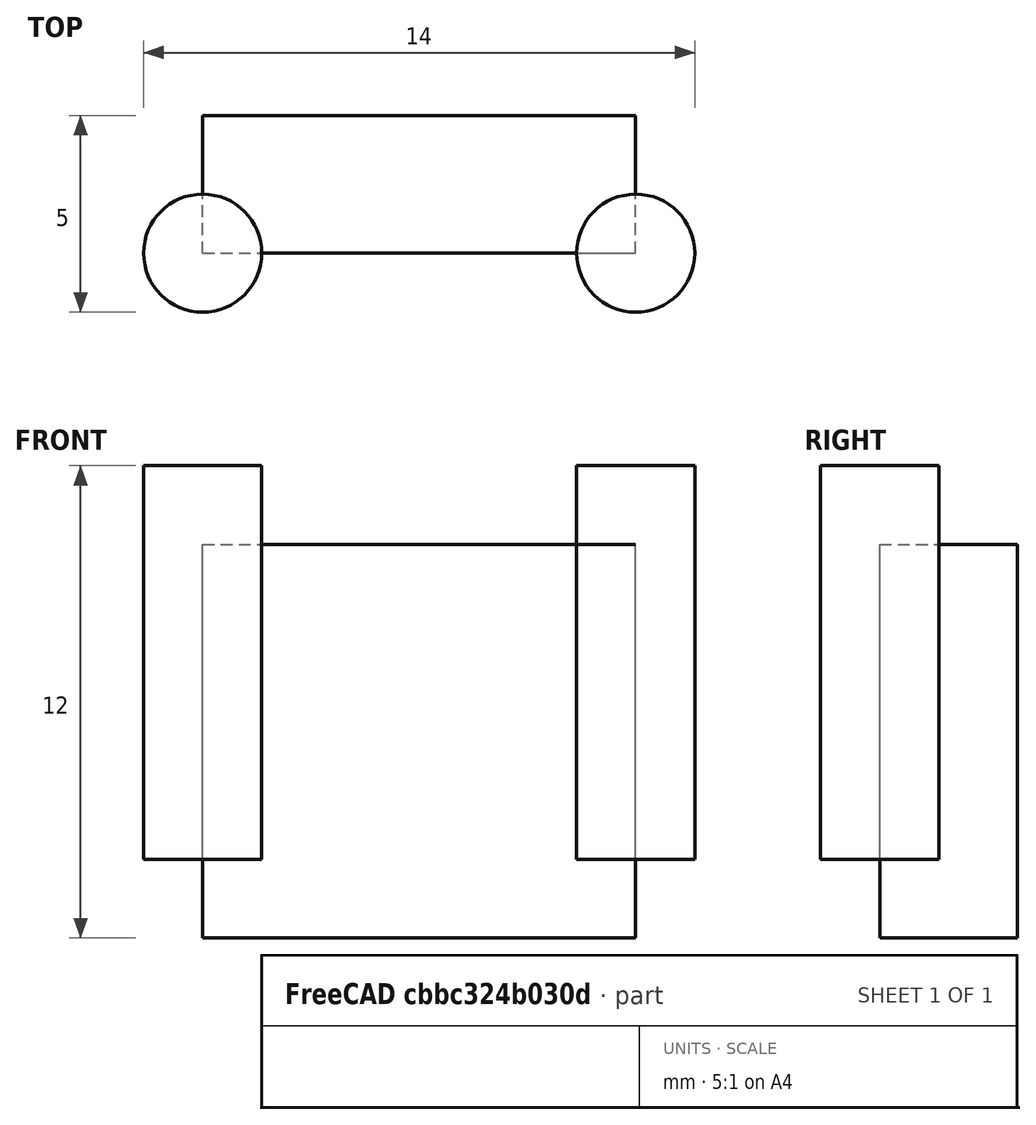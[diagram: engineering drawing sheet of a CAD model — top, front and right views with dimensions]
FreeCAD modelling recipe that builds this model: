
FCSTD DOCUMENT  (FreeCAD 0.18R14555 (Git shallow))
Label: y-rod-holder
License: All rights reserved
LicenseURL: http://en.wikipedia.org/wiki/All_rights_reserved
objects: Part::Cylinder×2, Mesh::Feature×1, Part::Feature×1, Part::Box×1
note: 4 computed .brp shape members not serialized (recipe doc carries the construction recipe); baked Part::Feature solids carry a one-line shape summary decoded from their .brp

FEATURE [Mesh::Feature] y_rod_holder  label="y-rod-holder"
FEATURE [Part::Feature] y_rod_holder001
  shape: bbox 26 x 14 x 10 mm, 2692 faces, 0 solids (baked)
FEATURE [Part::Cylinder] Cylinder
  Angle = 360
  AttacherType = Attacher::AttachEngine3D
  Height = 10
  Placement = pos=(5.5,-3.5,-4) rot=(0,0,1;0rad)
  Radius = 1.5
FEATURE [Part::Cylinder] Cylinder001
  Angle = 360
  AttacherType = Attacher::AttachEngine3D
  Height = 10
  Placement = pos=(-5.5,-3.5,-4) rot=(0,0,1;0rad)
  Radius = 1.5
FEATURE [Part::Box] Box001  label="Cube001"
  AttacherType = Attacher::AttachEngine3D
  Height = 10
  Length = 11
  Placement = pos=(-5.5,-3.5,-6) rot=(0,0,1;0rad)
  Width = 3.5
